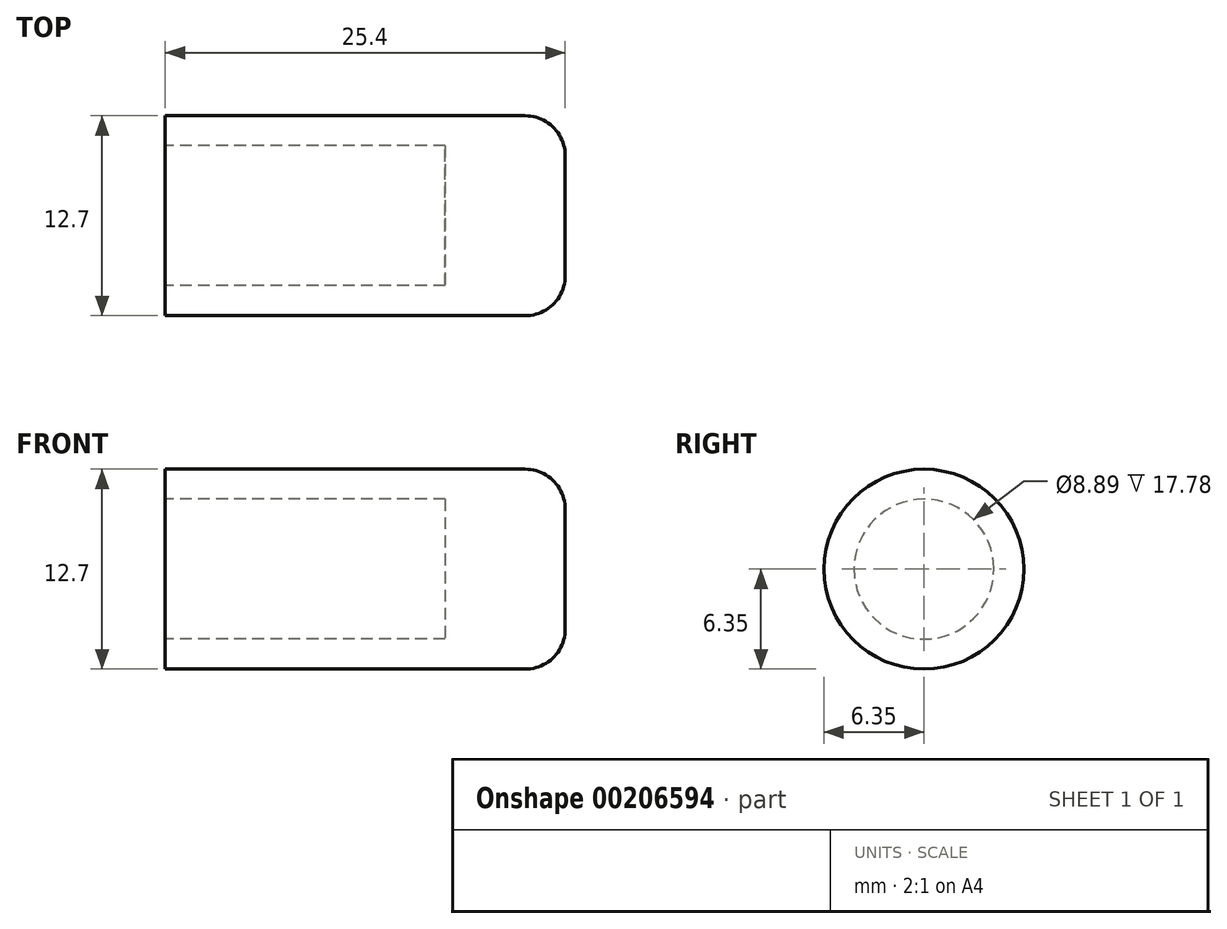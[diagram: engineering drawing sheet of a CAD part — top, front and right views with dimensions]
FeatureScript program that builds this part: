
annotation { "Feature Type Name" : "Feature", "Feature Type Description" : "" }
export const myFeature = defineFeature(function(context is Context, id is Id, definition is map)
    precondition{}
    {
        {
            var Q0;
            Q0=qCreatedBy(makeId("Right.planeOp"),FACE);
            var sketch = newSketch(context, id + "F0", { "sketchPlane" : qUnion([Q0])});
            skCircle(sketch, "E0", {"center": v(0, 0) * mm, "radius": 6.35 * mm});
            skSolve(sketch);
        }
        {
            var Q0;
            Q0=makeQuery(id+"F0.imprint","IMPRINT",FACE,{"disambiguationData":[TD([[makeQuery(id+"F0.imprint","IMPRINT",EDGE,{"derivedFrom":sQuery(id+"F0.wireOp",EDGE,"E0")}),1.0]])]});
            extrude(context, id + "F1", {"entities" : qUnion([Q0]), "depth" : 25.4 * mm});
        }
        {
            var Q0;
            Q0=makeQuery(id+"F1.opExtrude","CAP_FACE",FACE,{"disambiguationData":[OSD([sQuery(id+"F0.wireOp",EDGE,"E0")])],"isStart":true});
            var sketch = newSketch(context, id + "F2", { "sketchPlane" : qUnion([Q0])});
            skCircle(sketch, "E1", {"center": v(0, 0) * mm, "radius": 4.45 * mm});
            skSolve(sketch);
        }
        {
            var Q0;
            Q0=makeQuery(id+"F2.imprint","IMPRINT",FACE,{"disambiguationData":[TD([[makeQuery(id+"F2.imprint","IMPRINT",EDGE,{"derivedFrom":sQuery(id+"F2.wireOp",EDGE,"E1")}),1.0]])]});
            var Q1;
            Q1=sQuery(id+"F2.wireOp",EDGE,"E1");
            extrude(context, id + "F3", {"entities" : qUnion([Q0]), "operationType" : NewBodyOperationType.REMOVE, "surfaceEntities" : qUnion([Q1]), "oppositeDirection" : true, "depth" : 17.78 * mm});
        }
        {
            var Q0;
            Q0=makeQuery(id+"F1.opExtrude","CAP_EDGE",EDGE,{"disambiguationData":[OSD([sQuery(id+"F0.wireOp",EDGE,"E0")])],"isStart":false});
            fillet(context, id + "F4", {"entities" : qUnion([Q0]), "radius" : 2.54 * mm, "tangentPropagation" : true, "allowEdgeOverflow" : false});
        }
    });
